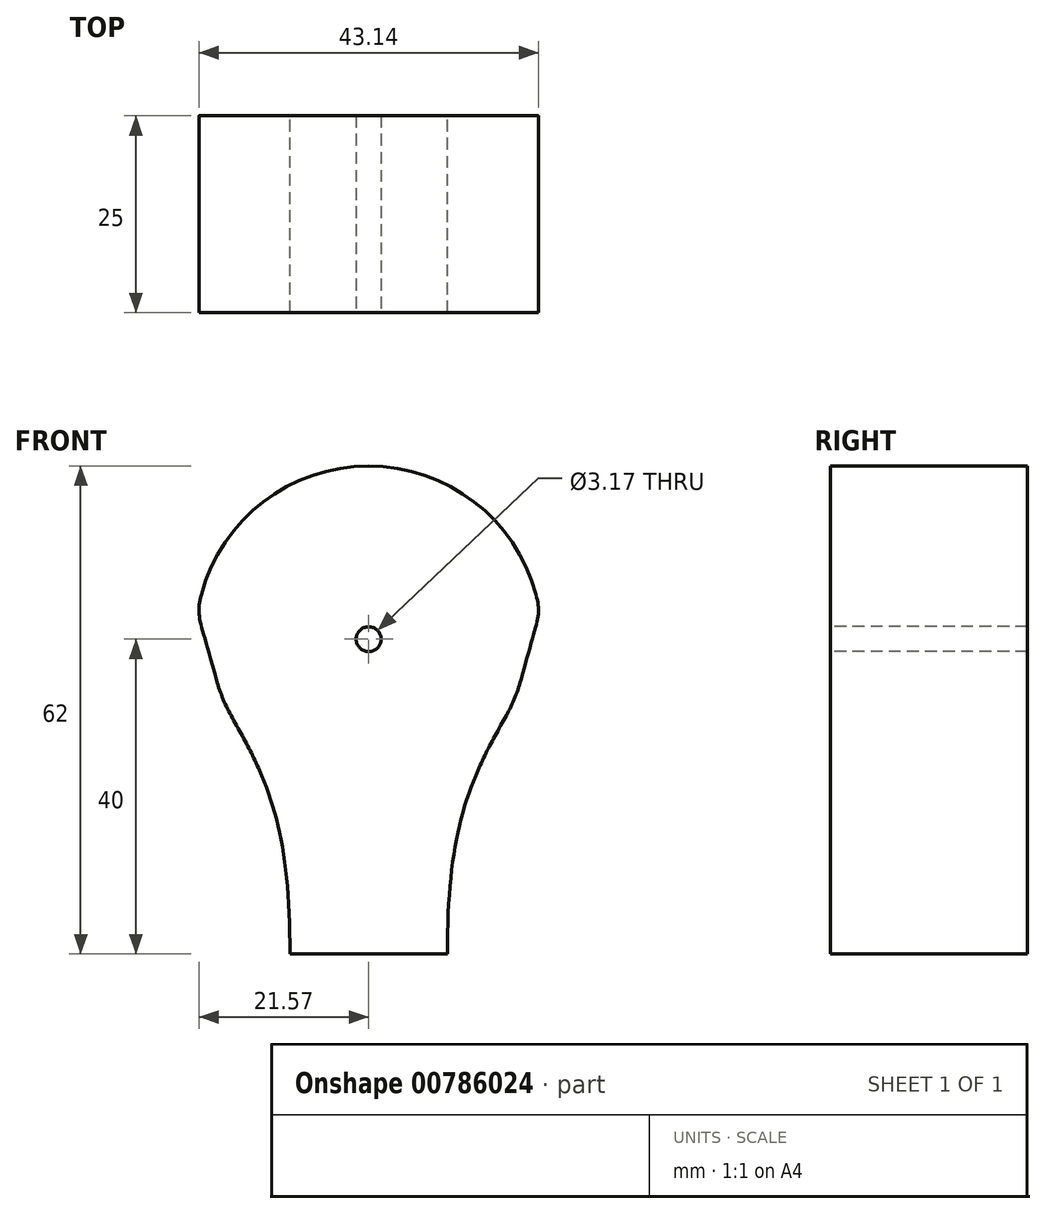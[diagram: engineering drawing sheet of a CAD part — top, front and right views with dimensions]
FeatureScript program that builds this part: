
annotation { "Feature Type Name" : "Feature", "Feature Type Description" : "" }
export const myFeature = defineFeature(function(context is Context, id is Id, definition is map)
    precondition{}
    {
        {
            var Q0;
            Q0=qCreatedBy(makeId("Front.planeOp"),FACE);
            var sketch = newSketch(context, id + "F0", { "sketchPlane" : qUnion([Q0])});
            skLineSegment(sketch, "E0.bottom", {"start": v(10, 0) * mm, "end": v(-10, 0) * mm, "construction": true});
            skLineSegment(sketch, "E0.top", {"start": v(10, -40) * mm, "end": v(-10, -40) * mm});
            skLineSegment(sketch, "E0.left", {"start": v(10, 0) * mm, "end": v(10, -40) * mm, "construction": true});
            skLineSegment(sketch, "E0.right", {"start": v(-10, 0) * mm, "end": v(-10, -40) * mm, "construction": true});
            skPoint(sketch, "E0.middle", {"position": v(0, -20) * mm});
            skCircle(sketch, "E1", {"center": v(0, 0) * mm, "radius": 20 * mm});
            skCircle(sketch, "E2", {"center": v(0, 0) * mm, "radius": 22 * mm});
            skLineSegment(sketch, "E3", {"start": v(0, 0) * mm, "end": v(21.25, 5.7) * mm});
            skLineSegment(sketch, "E4", {"start": v(0, 0) * mm, "end": v(19.32, -5.18) * mm});
            skLineSegment(sketch, "E5", {"start": v(0, 0) * mm, "end": v(17.32, -10) * mm});
            skLineSegment(sketch, "E6", {"start": v(0, 0) * mm, "end": v(19.05, 11) * mm});
            skFitSpline(sketch, "E7", {"points": [v(19.32, -5.18) * mm, v(21.25, 5.7) * mm], "startDerivative": vector(6.21, 23.18) * mm, "endDerivative": vector(-2.33, 8.7) * mm});
            skLineSegment(sketch, "E8", {"start": v(21.25, 5.7) * mm, "end": v(22.03, 2.8) * mm});
            skLineSegment(sketch, "E9", {"start": v(19.32, -5.18) * mm, "end": v(21.39, 2.55) * mm});
            skFitSpline(sketch, "E10", {"points": [v(17.32, -10) * mm, v(10, -40) * mm], "startDerivative": vector(-15, -25.98) * mm, "endDerivative": vector(0, -45) * mm});
            skLineSegment(sketch, "E11", {"start": v(17.32, -10) * mm, "end": v(12.32, -18.66) * mm});
            skLineSegment(sketch, "E12", {"start": v(0, -40) * mm, "end": v(0, 22) * mm, "construction": true});
            skFitSpline(sketch, "E13.MirrorCS", {"points": [v(-19.32, -5.18) * mm, v(-21.25, 5.7) * mm], "startDerivative": vector(-6.21, 23.18) * mm, "endDerivative": vector(2.33, 8.7) * mm});
            skFitSpline(sketch, "E14.MirrorCS", {"points": [v(-17.32, -10) * mm, v(-10, -40) * mm], "startDerivative": vector(15, -25.98) * mm, "endDerivative": vector(0, -45) * mm});
            skLineSegment(sketch, "E15.MirrorCS", {"start": v(0, 0) * mm, "end": v(-19.05, 11) * mm});
            skSolve(sketch);
        }
        {
            var Q0;
            {var subQ0=sQuery(id+"F0.wireOp",EDGE,"E6");var subQ1=sQuery(id+"F0.wireOp",EDGE,"E1");var subQ2=makeQuery(id+"F0.imprint","INTERSECT",VERTEX,{"derivedFrom":[subQ1,subQ0]});Q0=makeQuery(id+"F0.imprint","IMPRINT",FACE,{"disambiguationData":[TD([[makeQuery(id+"F0.imprint","IMPRINT",EDGE,{"disambiguationData":[TD([[subQ2,-1.0]])],"derivedFrom":subQ1}),1.0]])]});}
            var Q1;
            {var subQ0=sQuery(id+"F0.wireOp",EDGE,"E6");var subQ1=sQuery(id+"F0.wireOp",EDGE,"E1");var subQ2=makeQuery(id+"F0.imprint","INTERSECT",VERTEX,{"derivedFrom":[subQ1,subQ0]});Q1=makeQuery(id+"F0.imprint","IMPRINT",FACE,{"disambiguationData":[TD([[makeQuery(id+"F0.imprint","IMPRINT",EDGE,{"disambiguationData":[TD([[subQ2,-1.0]])],"derivedFrom":subQ1}),-1.0]])]});}
            var Q2;
            {var subQ0=sQuery(id+"F0.wireOp",EDGE,"E6");var subQ1=sQuery(id+"F0.wireOp",EDGE,"E1");var subQ2=makeQuery(id+"F0.imprint","INTERSECT",VERTEX,{"derivedFrom":[subQ1,subQ0]});Q2=makeQuery(id+"F0.imprint","IMPRINT",FACE,{"disambiguationData":[TD([[makeQuery(id+"F0.imprint","IMPRINT",EDGE,{"disambiguationData":[TD([[subQ2,1.0]])],"derivedFrom":subQ1}),-1.0]])]});}
            var Q3;
            {var subQ0=sQuery(id+"F0.wireOp",EDGE,"E6");var subQ1=sQuery(id+"F0.wireOp",EDGE,"E1");var subQ2=makeQuery(id+"F0.imprint","INTERSECT",VERTEX,{"derivedFrom":[subQ1,subQ0]});Q3=makeQuery(id+"F0.imprint","IMPRINT",FACE,{"disambiguationData":[TD([[makeQuery(id+"F0.imprint","IMPRINT",EDGE,{"disambiguationData":[TD([[subQ2,1.0]])],"derivedFrom":subQ1}),1.0]])]});}
            var Q4;
            {var subQ0=sQuery(id+"F0.wireOp",EDGE,"E4");Q4=makeQuery(id+"F0.imprint","IMPRINT",FACE,{"disambiguationData":[TD([[makeQuery(id+"F0.imprint","IMPRINT",EDGE,{"derivedFrom":subQ0}),1.0]])]});}
            var Q5;
            {var subQ0=sQuery(id+"F0.wireOp",EDGE,"E7");Q5=makeQuery(id+"F0.imprint","IMPRINT",FACE,{"disambiguationData":[TD([[makeQuery(id+"F0.imprint","IMPRINT",EDGE,{"derivedFrom":subQ0}),1.0]])]});}
            var Q6;
            {var subQ0=sQuery(id+"F0.wireOp",EDGE,"E4");Q6=makeQuery(id+"F0.imprint","IMPRINT",FACE,{"disambiguationData":[TD([[makeQuery(id+"F0.imprint","IMPRINT",EDGE,{"derivedFrom":subQ0}),-1.0]])]});}
            var Q7;
            {var subQ0=sQuery(id+"F0.wireOp",EDGE,"E5");Q7=makeQuery(id+"F0.imprint","IMPRINT",FACE,{"disambiguationData":[TD([[makeQuery(id+"F0.imprint","IMPRINT",EDGE,{"derivedFrom":subQ0}),-1.0]])]});}
            var Q8;
            {var subQ0=sQuery(id+"F0.wireOp",EDGE,"E0.top");Q8=makeQuery(id+"F0.imprint","IMPRINT",FACE,{"disambiguationData":[TD([[makeQuery(id+"F0.imprint","IMPRINT",EDGE,{"derivedFrom":subQ0}),-1.0]])]});}
            var Q9;
            {var subQ3=sQuery(id+"F0.wireOp",EDGE,"E14.MirrorCS");var subQ5=sQuery(id+"F0.wireOp",EDGE,"E2");var subQ6=makeQuery(id+"F0.imprint","INTERSECT",VERTEX,{"derivedFrom":[subQ5,subQ3]});Q9=makeQuery(id+"F0.imprint","IMPRINT",FACE,{"disambiguationData":[TD([[makeQuery(id+"F0.imprint","IMPRINT",EDGE,{"disambiguationData":[TD([[subQ6,-1.0]])],"derivedFrom":subQ5}),1.0]])]});}
            var Q10;
            {var subQ0=sQuery(id+"F0.wireOp",EDGE,"E13.MirrorCS");Q10=makeQuery(id+"F0.imprint","IMPRINT",FACE,{"disambiguationData":[TD([[makeQuery(id+"F0.imprint","IMPRINT",EDGE,{"derivedFrom":subQ0}),-1.0]])]});}
            var Q11;
            {var subQ0=sQuery(id+"F0.wireOp",EDGE,"E11");var subQ1=sQuery(id+"F0.wireOp",EDGE,"E2");var subQ2=makeQuery(id+"F0.imprint","INTERSECT",VERTEX,{"derivedFrom":[subQ1,subQ0]});Q11=makeQuery(id+"F0.imprint","IMPRINT",FACE,{"disambiguationData":[TD([[makeQuery(id+"F0.imprint","IMPRINT",EDGE,{"disambiguationData":[TD([[subQ2,-1.0]])],"derivedFrom":subQ1}),1.0]])]});}
            extrude(context, id + "F1", {"entities" : qUnion([Q0, Q1, Q2, Q3, Q4, Q5, Q6, Q7, Q8, Q9, Q10, Q11]), "depth" : 25 * mm, "offsetDistance" : 25 * mm});
        }
        {
            var Q0;
            Q0=makeQuery(id+"F1.opExtrude","CAP_FACE",FACE,{"disambiguationData":[OSD([sQuery(id+"F0.wireOp",EDGE,"E0.top"),sQuery(id+"F0.wireOp",EDGE,"E1"),sQuery(id+"F0.wireOp",EDGE,"E2"),sQuery(id+"F0.wireOp",EDGE,"E7"),sQuery(id+"F0.wireOp",EDGE,"E10"),sQuery(id+"F0.wireOp",EDGE,"E13.MirrorCS"),sQuery(id+"F0.wireOp",EDGE,"E14.MirrorCS")])],"isStart":false});
            var sketch = newSketch(context, id + "F2", { "sketchPlane" : qUnion([Q0])});
            skCircle(sketch, "E16", {"center": v(0, 0) * mm, "radius": 1.59 * mm});
            skSolve(sketch);
        }
        {
            var Q0;
            Q0=qSketchRegion(id+"F2",true);
            extrude(context, id + "F3", {"entities" : qUnion([Q0]), "operationType" : NewBodyOperationType.REMOVE, "oppositeDirection" : true, "depth" : 25 * mm, "offsetDistance" : 25 * mm});
        }
    });
